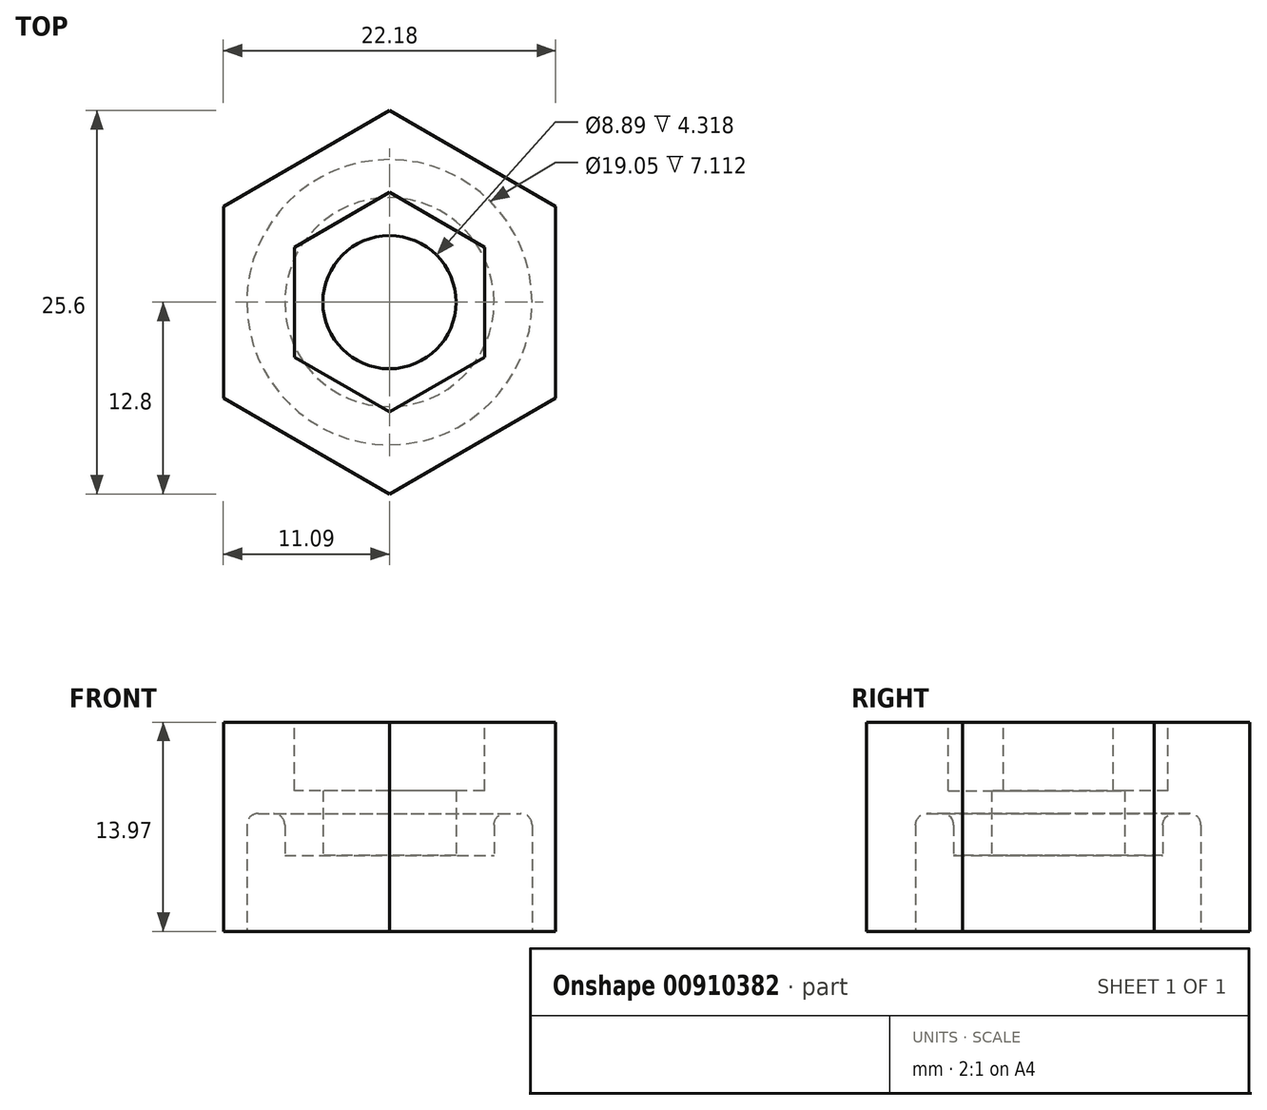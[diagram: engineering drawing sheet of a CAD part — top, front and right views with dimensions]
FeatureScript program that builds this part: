
annotation { "Feature Type Name" : "Feature", "Feature Type Description" : "" }
export const myFeature = defineFeature(function(context is Context, id is Id, definition is map)
    precondition{}
    {
        {
            var Q0;
            Q0=qCreatedBy(makeId("Top.planeOp"),FACE);
            var sketch = newSketch(context, id + "F0", { "sketchPlane" : qUnion([Q0])});
            skCircle(sketch, "E0.cCircle", {"center": v(0, 0) * mm, "radius": 11.09 * mm, "construction": true});
            skLineSegment(sketch, "E0.0", {"start": v(11.09, 6.4) * mm, "end": v(11.09, -6.4) * mm});
            skLineSegment(sketch, "E0.1", {"start": v(11.09, -6.4) * mm, "end": v(0, -12.8) * mm});
            skLineSegment(sketch, "E0.2", {"start": v(0, -12.8) * mm, "end": v(-11.09, -6.4) * mm});
            skLineSegment(sketch, "E0.3", {"start": v(-11.09, -6.4) * mm, "end": v(-11.09, 6.4) * mm});
            skLineSegment(sketch, "E0.4", {"start": v(-11.09, 6.4) * mm, "end": v(0, 12.8) * mm});
            skLineSegment(sketch, "E0.5", {"start": v(0, 12.8) * mm, "end": v(11.09, 6.4) * mm});
            skPoint(sketch, "E0.0.midPoint", {"position": v(11.09, 0) * mm});
            skCircle(sketch, "E1", {"center": v(0, 0) * mm, "radius": 4.45 * mm});
            skSolve(sketch);
        }
        {
            var Q0;
            Q0 = qSketchRegion(id + "F0", true);
            extrude(context, id + "F1", {"entities" : qUnion([Q0]), "depth" : 13.97 * mm, "offsetDistance" : 25.4 * mm});
        }
        {
            var Q0;
            Q0=makeQuery(id+"F1.opExtrude","CAP_FACE",FACE,{"disambiguationData":[OSD([sQuery(id+"F0.wireOp",EDGE,"E0.0"),sQuery(id+"F0.wireOp",EDGE,"E0.1"),sQuery(id+"F0.wireOp",EDGE,"E0.2"),sQuery(id+"F0.wireOp",EDGE,"E0.3"),sQuery(id+"F0.wireOp",EDGE,"E0.4"),sQuery(id+"F0.wireOp",EDGE,"E0.5")])],"isStart":true});
            var sketch = newSketch(context, id + "F2", { "sketchPlane" : qUnion([Q0])});
            skCircle(sketch, "E2", {"center": v(0, 0) * mm, "radius": 9.53 * mm});
            skCircle(sketch, "E3", {"center": v(0, 0) * mm, "radius": 6.99 * mm});
            skSolve(sketch);
        }
        {
            var Q0;
            Q0 = qSketchRegion(id + "F2", true);
            extrude(context, id + "F3", {"entities" : qUnion([Q0]), "operationType" : NewBodyOperationType.REMOVE, "oppositeDirection" : true, "depth" : 7.87 * mm, "offsetDistance" : 25.4 * mm});
        }
        {
            var Q0;
            Q0=makeQuery(id+"F1.opExtrude","CAP_FACE",FACE,{"disambiguationData":[OSD([sQuery(id+"F0.wireOp",EDGE,"E0.0"),sQuery(id+"F0.wireOp",EDGE,"E0.1"),sQuery(id+"F0.wireOp",EDGE,"E0.2"),sQuery(id+"F0.wireOp",EDGE,"E0.3"),sQuery(id+"F0.wireOp",EDGE,"E0.4"),sQuery(id+"F0.wireOp",EDGE,"E0.5"),sQuery(id+"F0.wireOp",EDGE,"E1")])],"isStart":false});
            var sketch = newSketch(context, id + "F4", { "sketchPlane" : qUnion([Q0])});
            skCircle(sketch, "E4.cCircle", {"center": v(0, 0) * mm, "radius": 6.35 * mm, "construction": true});
            skLineSegment(sketch, "E4.0", {"start": v(-6.35, -3.67) * mm, "end": v(-6.35, 3.67) * mm});
            skLineSegment(sketch, "E4.1", {"start": v(-6.35, 3.67) * mm, "end": v(0, 7.33) * mm});
            skLineSegment(sketch, "E4.2", {"start": v(0, 7.33) * mm, "end": v(6.35, 3.67) * mm});
            skLineSegment(sketch, "E4.3", {"start": v(6.35, 3.67) * mm, "end": v(6.35, -3.67) * mm});
            skLineSegment(sketch, "E4.4", {"start": v(6.35, -3.67) * mm, "end": v(0, -7.33) * mm});
            skLineSegment(sketch, "E4.5", {"start": v(0, -7.33) * mm, "end": v(-6.35, -3.67) * mm});
            skPoint(sketch, "E4.0.midPoint", {"position": v(-6.35, 0) * mm});
            skSolve(sketch);
        }
        {
            var Q0;
            Q0 = qSketchRegion(id + "F4", true);
            extrude(context, id + "F5", {"entities" : qUnion([Q0]), "operationType" : NewBodyOperationType.REMOVE, "oppositeDirection" : true, "depth" : 4.57 * mm, "offsetDistance" : 25.4 * mm});
        }
        {
            var Q0;
            Q0=makeQuery(id+"F3.boolean.opBoolean","COPY",FACE,{"derivedFrom":makeQuery(id+"F3.opExtrude","CAP_FACE",FACE,{"disambiguationData":[OSD([sQuery(id+"F2.wireOp",EDGE,"E2"),sQuery(id+"F2.wireOp",EDGE,"E3")])],"isStart":false})});
            fillet(context, id + "F6", {"entities" : qUnion([Q0]), "radius" : 0.76 * mm, "tangentPropagation" : true, "allowEdgeOverflow" : false});
        }
        {
            var Q0;
            {var subQ0=sQuery(id+"F0.wireOp",EDGE,"E1");Q0=makeQuery(id+"F3.boolean.opBoolean","SPLIT",FACE,{"disambiguationData":[TD([makeQuery(id+"F1.opExtrude","SWEPT_FACE",FACE,{"disambiguationData":[OSD([subQ0])]})])],"derivedFrom":makeQuery(id+"F1.opExtrude","CAP_FACE",FACE,{"disambiguationData":[OSD([sQuery(id+"F0.wireOp",EDGE,"E0.0"),sQuery(id+"F0.wireOp",EDGE,"E0.1"),sQuery(id+"F0.wireOp",EDGE,"E0.2"),sQuery(id+"F0.wireOp",EDGE,"E0.3"),sQuery(id+"F0.wireOp",EDGE,"E0.4"),sQuery(id+"F0.wireOp",EDGE,"E0.5"),subQ0])],"isStart":true})});}
            extrude(context, id + "F7", {"entities" : qUnion([Q0]), "operationType" : NewBodyOperationType.REMOVE, "oppositeDirection" : true, "depth" : 5.08 * mm, "offsetDistance" : 25.4 * mm});
        }
    });
